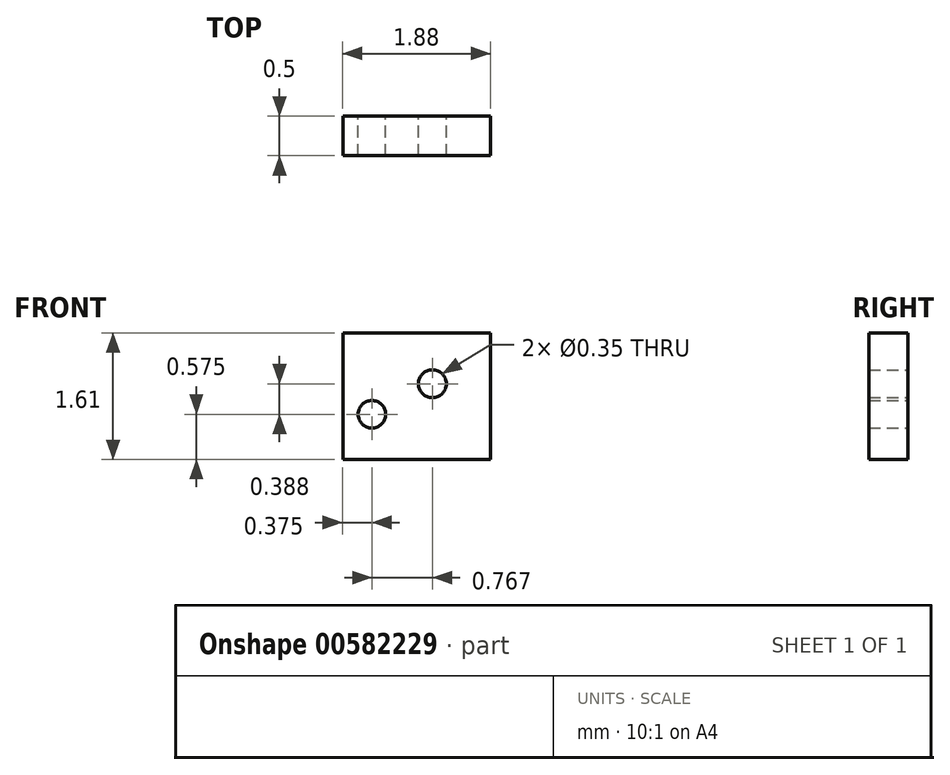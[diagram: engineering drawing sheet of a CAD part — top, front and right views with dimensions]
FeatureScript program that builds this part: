
annotation { "Feature Type Name" : "Feature", "Feature Type Description" : "" }
export const myFeature = defineFeature(function(context is Context, id is Id, definition is map)
    precondition{}
    {
        {
            var Q0;
            Q0=qCreatedBy(makeId("Front.planeOp"),FACE);
            var sketch = newSketch(context, id + "F0", { "sketchPlane" : qUnion([Q0])});
            skLineSegment(sketch, "E0.bottom", {"start": v(0, 0) * mm, "end": v(-1.88, 0) * mm});
            skLineSegment(sketch, "E0.top", {"start": v(0, 1.61) * mm, "end": v(-1.88, 1.61) * mm});
            skLineSegment(sketch, "E0.left", {"start": v(0, 0) * mm, "end": v(0, 1.61) * mm});
            skLineSegment(sketch, "E0.right", {"start": v(-1.88, 0) * mm, "end": v(-1.88, 1.6) * mm});
            skCircle(sketch, "E1", {"center": v(-1.5, 0.57) * mm, "radius": 0.17 * mm});
            skCircle(sketch, "E2", {"center": v(-0.74, 0.96) * mm, "radius": 0.18 * mm});
            skSolve(sketch);
        }
        {
            var Q0;
            Q0=makeQuery(id+"F0.imprint","IMPRINT",FACE,{"disambiguationData":[TD([[makeQuery(id+"F0.imprint","IMPRINT",EDGE,{"derivedFrom":sQuery(id+"F0.wireOp",EDGE,"E0.bottom")}),-1.0]])]});
            extrude(context, id + "F1", {"entities" : qUnion([Q0]), "depth" : 0.5 * mm, "offsetDistance" : 25 * mm});
        }
    });
